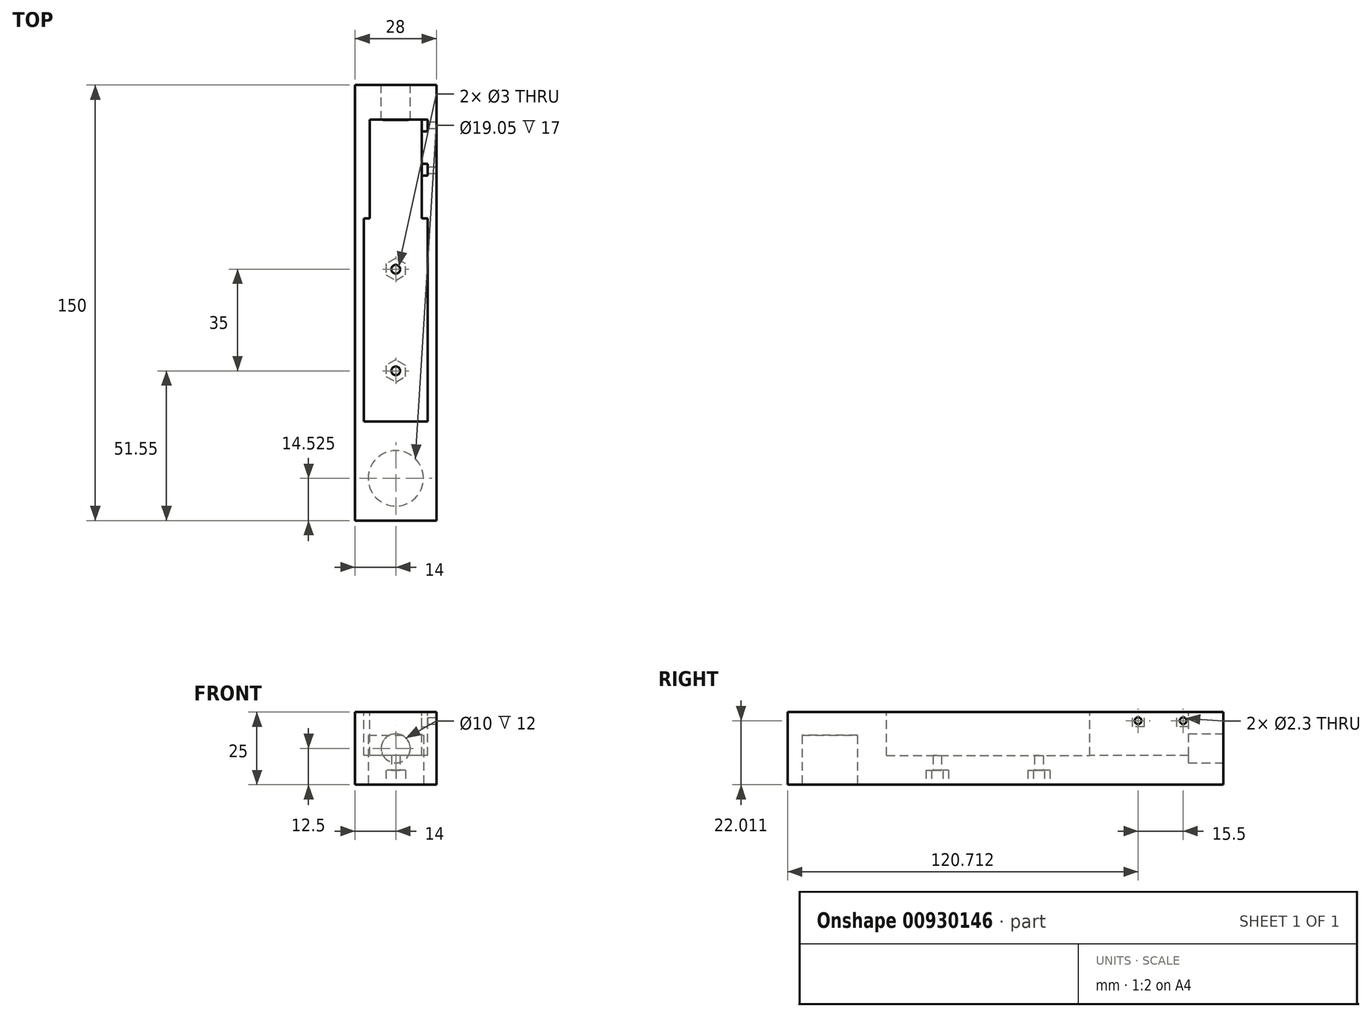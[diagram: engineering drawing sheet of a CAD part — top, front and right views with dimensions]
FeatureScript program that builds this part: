
annotation { "Feature Type Name" : "Feature", "Feature Type Description" : "" }
export const myFeature = defineFeature(function(context is Context, id is Id, definition is map)
    precondition{}
    {
        {
            var Q0;
            Q0=qCreatedBy(makeId("Front.planeOp"),FACE);
            var sketch = newSketch(context, id + "F0", { "sketchPlane" : qUnion([Q0])});
            skLineSegment(sketch, "E0.bottom", {"start": v(-14, 12.5) * mm, "end": v(14, 12.5) * mm});
            skLineSegment(sketch, "E0.top", {"start": v(-14, -12.5) * mm, "end": v(14, -12.5) * mm});
            skLineSegment(sketch, "E0.left", {"start": v(-14, 12.5) * mm, "end": v(-14, -12.5) * mm});
            skLineSegment(sketch, "E0.right", {"start": v(14, 12.5) * mm, "end": v(14, -12.5) * mm});
            skSolve(sketch);
        }
        {
            var Q0;
            Q0=makeQuery(id+"F0.imprint","IMPRINT",FACE,{"disambiguationData":[TD([[makeQuery(id+"F0.imprint","IMPRINT",EDGE,{"derivedFrom":sQuery(id+"F0.wireOp",EDGE,"E0.bottom")}),-1.0]])]});
            extrude(context, id + "F1", {"entities" : qUnion([Q0]), "oppositeDirection" : true, "depth" : 150 * mm, "offsetDistance" : 25 * mm});
        }
        {
            var Q0;
            Q0=makeQuery(id+"F1.opExtrude","SWEPT_FACE",FACE,{"disambiguationData":[OSD([sQuery(id+"F0.wireOp",EDGE,"E0.top")])]});
            var sketch = newSketch(context, id + "F2", { "sketchPlane" : qUnion([Q0])});
            skCircle(sketch, "E1", {"center": v(0, -14.53) * mm, "radius": 9.53 * mm});
            skSolve(sketch);
        }
        {
            var Q0;
            Q0=qSketchRegion(id+"F2",true);
            extrude(context, id + "F3", {"entities" : qUnion([Q0]), "operationType" : NewBodyOperationType.REMOVE, "oppositeDirection" : true, "depth" : 17 * mm, "offsetDistance" : 25 * mm});
        }
        {
            var Q0;
            Q0=makeQuery(id+"F1.opExtrude","SWEPT_FACE",FACE,{"disambiguationData":[OSD([sQuery(id+"F0.wireOp",EDGE,"E0.top")])]});
            var sketch = newSketch(context, id + "F4", { "sketchPlane" : qUnion([Q0])});
            skCircle(sketch, "E2", {"center": v(0, -51.55) * mm, "radius": 3.32 * mm});
            skCircle(sketch, "E3.cCircle", {"center": v(0, -51.55) * mm, "radius": 3.32 * mm, "construction": true});
            skLineSegment(sketch, "E3.0", {"start": v(3.32, -49.63) * mm, "end": v(3.32, -53.47) * mm});
            skLineSegment(sketch, "E3.1", {"start": v(3.32, -53.47) * mm, "end": v(0, -55.38) * mm});
            skLineSegment(sketch, "E3.2", {"start": v(0, -55.38) * mm, "end": v(-3.32, -53.47) * mm});
            skLineSegment(sketch, "E3.3", {"start": v(-3.32, -53.47) * mm, "end": v(-3.32, -49.63) * mm});
            skLineSegment(sketch, "E3.4", {"start": v(-3.32, -49.63) * mm, "end": v(0, -47.72) * mm});
            skLineSegment(sketch, "E3.5", {"start": v(0, -47.72) * mm, "end": v(3.32, -49.63) * mm});
            skPoint(sketch, "E3.0.midPoint", {"position": v(3.32, -51.55) * mm});
            skCircle(sketch, "E4", {"center": v(0, -51.55) * mm, "radius": 1.5 * mm});
            skCircle(sketch, "E5", {"center": v(0, -86.55) * mm, "radius": 3.32 * mm});
            skCircle(sketch, "E6.cCircle", {"center": v(0, -86.55) * mm, "radius": 3.32 * mm, "construction": true});
            skLineSegment(sketch, "E6.0", {"start": v(3.32, -84.63) * mm, "end": v(3.32, -88.47) * mm});
            skLineSegment(sketch, "E6.1", {"start": v(3.32, -88.47) * mm, "end": v(0, -90.38) * mm});
            skLineSegment(sketch, "E6.2", {"start": v(0, -90.38) * mm, "end": v(-3.32, -88.47) * mm});
            skLineSegment(sketch, "E6.3", {"start": v(-3.32, -88.47) * mm, "end": v(-3.32, -84.63) * mm});
            skLineSegment(sketch, "E6.4", {"start": v(-3.32, -84.63) * mm, "end": v(0, -82.72) * mm});
            skLineSegment(sketch, "E6.5", {"start": v(0, -82.72) * mm, "end": v(3.32, -84.63) * mm});
            skPoint(sketch, "E6.0.midPoint", {"position": v(3.32, -86.55) * mm});
            skCircle(sketch, "E7", {"center": v(0, -86.55) * mm, "radius": 1.5 * mm});
            skSolve(sketch);
        }
        {
            var Q0;
            Q0=qSketchRegion(id+"F4",true);
            extrude(context, id + "F5", {"entities" : qUnion([Q0]), "operationType" : NewBodyOperationType.REMOVE, "oppositeDirection" : true, "depth" : 5 * mm, "offsetDistance" : 25 * mm});
        }
        {
            var Q0;
            {var subQ1=sQuery(id+"F0.wireOp",EDGE,"E0.left");var subQ2=sQuery(id+"F0.wireOp",EDGE,"E0.top");Q0=makeQuery(id+"F5.boolean.opBoolean","SPLIT",FACE,{"disambiguationData":[TD([makeQuery(id+"F1.opExtrude","SWEPT_FACE",FACE,{"disambiguationData":[OSD([subQ1])]})])],"derivedFrom":makeQuery(id+"F1.opExtrude","SWEPT_FACE",FACE,{"disambiguationData":[OSD([subQ2])]})});}
            var sketch = newSketch(context, id + "F6", { "sketchPlane" : qUnion([Q0])});
            skCircle(sketch, "E8", {"center": v(0, -51.55) * mm, "radius": 1.5 * mm});
            skPoint(sketch, "E8.centerSnap0", {"position": v(3.32, -51.55) * mm});
            skCircle(sketch, "E9", {"center": v(0, -86.55) * mm, "radius": 1.5 * mm});
            skPoint(sketch, "E9.centerSnap0", {"position": v(-3.32, -86.55) * mm});
            skSolve(sketch);
        }
        {
            var Q0;
            Q0=qSketchRegion(id+"F6",true);
            extrude(context, id + "F7", {"entities" : qUnion([Q0]), "operationType" : NewBodyOperationType.REMOVE, "endBound" : BoundingType.THROUGH_ALL, "oppositeDirection" : true, "depth" : 25 * mm, "offsetDistance" : 25 * mm});
        }
        {
            var Q0;
            Q0=makeQuery(id+"F1.opExtrude","SWEPT_FACE",FACE,{"disambiguationData":[OSD([sQuery(id+"F0.wireOp",EDGE,"E0.bottom")])]});
            var sketch = newSketch(context, id + "F8", { "sketchPlane" : qUnion([Q0])});
            skLineSegment(sketch, "E10.bottom", {"start": v(11, 34.05) * mm, "end": v(-11, 34.05) * mm});
            skLineSegment(sketch, "E10.top", {"start": v(11, 104.05) * mm, "end": v(-11, 104.05) * mm});
            skLineSegment(sketch, "E10.left", {"start": v(11, 34.05) * mm, "end": v(11, 104.05) * mm});
            skLineSegment(sketch, "E10.right", {"start": v(-11, 34.05) * mm, "end": v(-11, 104.05) * mm});
            skSolve(sketch);
        }
        {
            var Q0;
            Q0=qSketchRegion(id+"F8",true);
            extrude(context, id + "F9", {"entities" : qUnion([Q0]), "operationType" : NewBodyOperationType.REMOVE, "oppositeDirection" : true, "depth" : 15 * mm, "offsetDistance" : 25 * mm});
        }
        {
            var Q0;
            Q0=makeQuery(id+"F1.opExtrude","SWEPT_FACE",FACE,{"disambiguationData":[OSD([sQuery(id+"F0.wireOp",EDGE,"E0.right")])]});
            var sketch = newSketch(context, id + "F10", { "sketchPlane" : qUnion([Q0])});
            skCircle(sketch, "E11", {"center": v(120.71, 9.51) * mm, "radius": 1.15 * mm});
            skCircle(sketch, "E12", {"center": v(136.21, 9.51) * mm, "radius": 1.15 * mm});
            skLineSegment(sketch, "E13.bottom", {"start": v(118.96, 11.66) * mm, "end": v(137.96, 11.66) * mm});
            skLineSegment(sketch, "E13.top", {"start": v(118.96, 7.36) * mm, "end": v(137.96, 7.36) * mm});
            skLineSegment(sketch, "E13.left", {"start": v(118.96, 11.66) * mm, "end": v(118.96, 7.36) * mm});
            skLineSegment(sketch, "E13.right", {"start": v(137.96, 11.66) * mm, "end": v(137.96, 7.36) * mm});
            skLineSegment(sketch, "E14.bottom", {"start": v(122.87, 12.5) * mm, "end": v(134.06, 12.5) * mm});
            skLineSegment(sketch, "E14.top", {"start": v(122.87, 6.61) * mm, "end": v(134.06, 6.61) * mm});
            skLineSegment(sketch, "E14.left", {"start": v(122.87, 12.5) * mm, "end": v(122.87, 6.61) * mm});
            skLineSegment(sketch, "E14.right", {"start": v(134.06, 12.5) * mm, "end": v(134.06, 6.61) * mm});
            skSolve(sketch);
        }
        {
            var Q0;
            Q0=makeQuery(id+"F10.imprint","IMPRINT",FACE,{"disambiguationData":[TD([[makeQuery(id+"F10.imprint","IMPRINT",EDGE,{"derivedFrom":sQuery(id+"F10.wireOp",EDGE,"E12")}),1.0]])]});
            var Q1;
            Q1=makeQuery(id+"F10.imprint","IMPRINT",FACE,{"disambiguationData":[TD([[makeQuery(id+"F10.imprint","IMPRINT",EDGE,{"derivedFrom":sQuery(id+"F10.wireOp",EDGE,"E11")}),1.0]])]});
            extrude(context, id + "F11", {"entities" : qUnion([Q0, Q1]), "operationType" : NewBodyOperationType.REMOVE, "oppositeDirection" : true, "depth" : 5 * mm, "offsetDistance" : 25 * mm});
        }
        {
            var Q0;
            Q0=makeQuery(id+"F8.imprint","IMPRINT",FACE,{"disambiguationData":[TD([[makeQuery(id+"F8.imprint","IMPRINT",EDGE,{"derivedFrom":sQuery(id+"F8.wireOp",EDGE,"E10.bottom")}),1.0]])]});
            var sketch = newSketch(context, id + "F12", { "sketchPlane" : qUnion([Q0])});
            skLineSegment(sketch, "E15.bottom", {"start": v(9, 122.84) * mm, "end": v(11, 122.84) * mm});
            skLineSegment(sketch, "E15.top", {"start": v(9, 118.82) * mm, "end": v(11, 118.82) * mm});
            skLineSegment(sketch, "E15.left", {"start": v(9, 122.84) * mm, "end": v(9, 118.82) * mm});
            skLineSegment(sketch, "E15.right", {"start": v(11, 122.84) * mm, "end": v(11, 118.82) * mm});
            skLineSegment(sketch, "E16.bottom", {"start": v(9, 138.1) * mm, "end": v(11, 138.1) * mm});
            skLineSegment(sketch, "E16.top", {"start": v(9, 134.07) * mm, "end": v(11, 134.07) * mm});
            skLineSegment(sketch, "E16.left", {"start": v(9, 138.1) * mm, "end": v(9, 134.07) * mm});
            skLineSegment(sketch, "E16.right", {"start": v(11, 138.1) * mm, "end": v(11, 134.07) * mm});
            skSolve(sketch);
        }
        {
            var Q0;
            Q0=qSketchRegion(id+"F12",true);
            extrude(context, id + "F13", {"entities" : qUnion([Q0]), "operationType" : NewBodyOperationType.REMOVE, "oppositeDirection" : true, "depth" : 5 * mm, "offsetDistance" : 25 * mm});
        }
        {
            var Q0;
            Q0=makeQuery(id+"F8.imprint","IMPRINT",FACE,{"disambiguationData":[TD([[makeQuery(id+"F8.imprint","IMPRINT",EDGE,{"derivedFrom":sQuery(id+"F8.wireOp",EDGE,"E10.bottom")}),1.0]])]});
            var sketch = newSketch(context, id + "F14", { "sketchPlane" : qUnion([Q0])});
            skLineSegment(sketch, "E17.bottom", {"start": v(9, 138.1) * mm, "end": v(-9, 138.1) * mm});
            skLineSegment(sketch, "E17.top", {"start": v(9, 118.82) * mm, "end": v(-9, 118.82) * mm});
            skLineSegment(sketch, "E17.left", {"start": v(9, 138.1) * mm, "end": v(9, 118.82) * mm});
            skLineSegment(sketch, "E17.right", {"start": v(-9, 138.1) * mm, "end": v(-9, 118.82) * mm});
            skSolve(sketch);
        }
        {
            var Q0;
            Q0=qSketchRegion(id+"F14",true);
            extrude(context, id + "F15", {"entities" : qUnion([Q0]), "operationType" : NewBodyOperationType.REMOVE, "oppositeDirection" : true, "depth" : 15 * mm, "offsetDistance" : 25 * mm});
        }
        {
            var Q0;
            Q0=makeQuery(id+"F14.imprint","IMPRINT",FACE,{"disambiguationData":[TD([[makeQuery(id+"F14.imprint","IMPRINT",EDGE,{"derivedFrom":sQuery(id+"F14.wireOp",EDGE,"E17.bottom")}),-1.0]])]});
            var sketch = newSketch(context, id + "F16", { "sketchPlane" : qUnion([Q0])});
            skLineSegment(sketch, "E18.bottom", {"start": v(9, 118.82) * mm, "end": v(-9, 118.82) * mm});
            skLineSegment(sketch, "E18.top", {"start": v(9, 104.05) * mm, "end": v(-9, 104.05) * mm});
            skLineSegment(sketch, "E18.left", {"start": v(9, 118.82) * mm, "end": v(9, 104.05) * mm});
            skLineSegment(sketch, "E18.right", {"start": v(-9, 118.82) * mm, "end": v(-9, 104.05) * mm});
            skSolve(sketch);
        }
        {
            var Q0;
            Q0=qSketchRegion(id+"F16",true);
            extrude(context, id + "F17", {"entities" : qUnion([Q0]), "operationType" : NewBodyOperationType.REMOVE, "oppositeDirection" : true, "depth" : 15 * mm, "offsetDistance" : 25 * mm});
        }
        {
            var Q0;
            Q0=makeQuery(id+"F1.opExtrude","CAP_FACE",FACE,{"disambiguationData":[OSD([sQuery(id+"F0.wireOp",EDGE,"E0.bottom"),sQuery(id+"F0.wireOp",EDGE,"E0.top"),sQuery(id+"F0.wireOp",EDGE,"E0.left"),sQuery(id+"F0.wireOp",EDGE,"E0.right")])],"isStart":false});
            var sketch = newSketch(context, id + "F18", { "sketchPlane" : qUnion([Q0])});
            skCircle(sketch, "E19", {"center": v(0, 0) * mm, "radius": 5 * mm});
            skSolve(sketch);
        }
        {
            var Q0;
            Q0=qSketchRegion(id+"F18",true);
            extrude(context, id + "F19", {"entities" : qUnion([Q0]), "operationType" : NewBodyOperationType.REMOVE, "oppositeDirection" : true, "depth" : 12 * mm, "offsetDistance" : 25 * mm});
        }
        {
            var Q0;
            Q0=sQuery(id+"F10.wireOp",EDGE,"E14.right");
            var Q1;
            Q1=sQuery(id+"F10.wireOp",EDGE,"E14.left");
            var Q2;
            Q2=sQuery(id+"F10.wireOp",EDGE,"E14.top");
            var Q3;
            Q3=sQuery(id+"F10.wireOp",EDGE,"E14.bottom");
            extrude(context, id + "F20", {"bodyType" : ToolBodyType.SURFACE, "surfaceEntities" : qUnion([Q0, Q1, Q2, Q3]), "oppositeDirection" : true, "depth" : 10 * mm, "offsetDistance" : 25 * mm});
        }
    });
